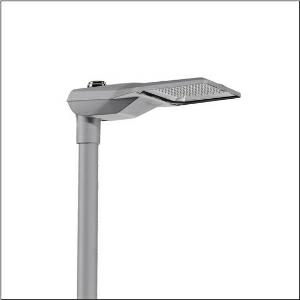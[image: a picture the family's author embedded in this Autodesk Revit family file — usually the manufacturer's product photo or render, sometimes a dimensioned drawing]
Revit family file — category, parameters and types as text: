
# Revit family: streetlight_sl_21_midi___st1_0a_5xe7d57n08mb_4ce1
name_source: partatom
category: Lighting Fixtures
units: mm (PartAtom-declared; Revit-internal decimal feet)

## family parameters
Cut with Voids When Loaded = No
Host = Face
Light Source = No
Part Type = Normal
Room Calculation Point = No
Round Connector Dimension = Use Diameter
Shared = No

## types (1)
- --- (1 x LED, 15800 lm, 137 W, 3000K)
    Apparent Load = 137 VA
    CIE Flux Codes = 37 72 97 100 100
    Color Rendering = 80
    Color Temperature = 3000K
    Default Elevation = 1800 mm
    Description = Streetlight SL 21 midi, mast luminaire, primary light control with lens, of PMMA, primary optical cover: cover, of toughened safety glass, transparent, light distribution: ST1.0a, light emission: direct distribution, primary light characteristic: asymmetric, installation type: side-entry, LED, 3G 2.5mm², High Power LED, rated luminous flux: 15.800lm, luminous efficacy: 115lm/W, light colour: 830, colour temperature: 3000K, control gear: NEMA (7pin), control: overheat protection, pre-setting: linear dimming characteristic, constant luminous flux control, time-dependent luminous flux control, flexible luminous flux parameterisation, mains connection: 220..240V, AC, 50/60Hz, connection cable pre-assembled, cable length: 12,5m, wiring characteristics: H05VV-F, start of lifetime: 137W, end of service life: 144W, reduction: 61W, luminaire housing, of diecast aluminium (EN AC-44300), powder-coated, Siteco® metallic grey (DB 702S), corrosivity category C5 mid according to DIN EN ISO 12944, multi-level sealing system, sealing non-destructively replaceable, inclination adjustable: 0°, 5°, 10°, 15°, length: 644mm, width: 335mm, height: 110mm, spigot size: 42mm (side-entry), mounting height: 4..8m, protection rating (complete): IP66, insulation class (complete): insulation class I (protective earthing), certification: CE, ENEC, ENEC+, VDE, impact resistance: IK10, permissible operating ambient temperature for outdoor applications: -40..+50°C, standard-compliant lighting for roads and squares, packaging unit: 1 piece

Light Distribution: ST1.0a
    Height = 111 mm
    Lamp = 1 x LED
    Lamp Light Flux = 15800 lm
    Lamp Power = 137 W
    Lamp count = 1
    Length = 644 mm
    Luminous efficacy = 115 lm/W
    Manufacturer = Siteco
    ModVariant = No
    Model = 5XE7D57N08MB
    Number of Poles = 1
    OnlyDefault = Yes
    Power Factor = 1
    Product Name = Streetlight SL 21 midi | ST1.0a
    Product group = mast luminaire | pylon top
    ProductGroupID = 6100
    Protection Class = Protection class I
    Protection Degree = IP 66
    RLX_Detail_Level = 1
    RLX_Emergency_Light_Flux = 0 lm
    RLX_Emergency_Type = 0
    RLX_Emergency_Type_DB = No
    RlxData = <blob elided: 26497 chars, md5=ac7eda57>
    Socket = socket
    Standby Power = 0 W
    System Light Flux = 15800 lm
    System Power = 137 W
    Type Comments = factory setting: luminous flux: 100 % | dim-lin: 254 | 700 mA
    Type Image = l_1294377.jpg
    URL = http://relux.com
    VarID = @adj_157411
    Voltage = 0 V
    Weight = 0.00 kg
    Width = 336 mm

## geometry (parser evidence)
native form markers: Blend x4, Sweep x10
no freeform markers — native parametric forms only
